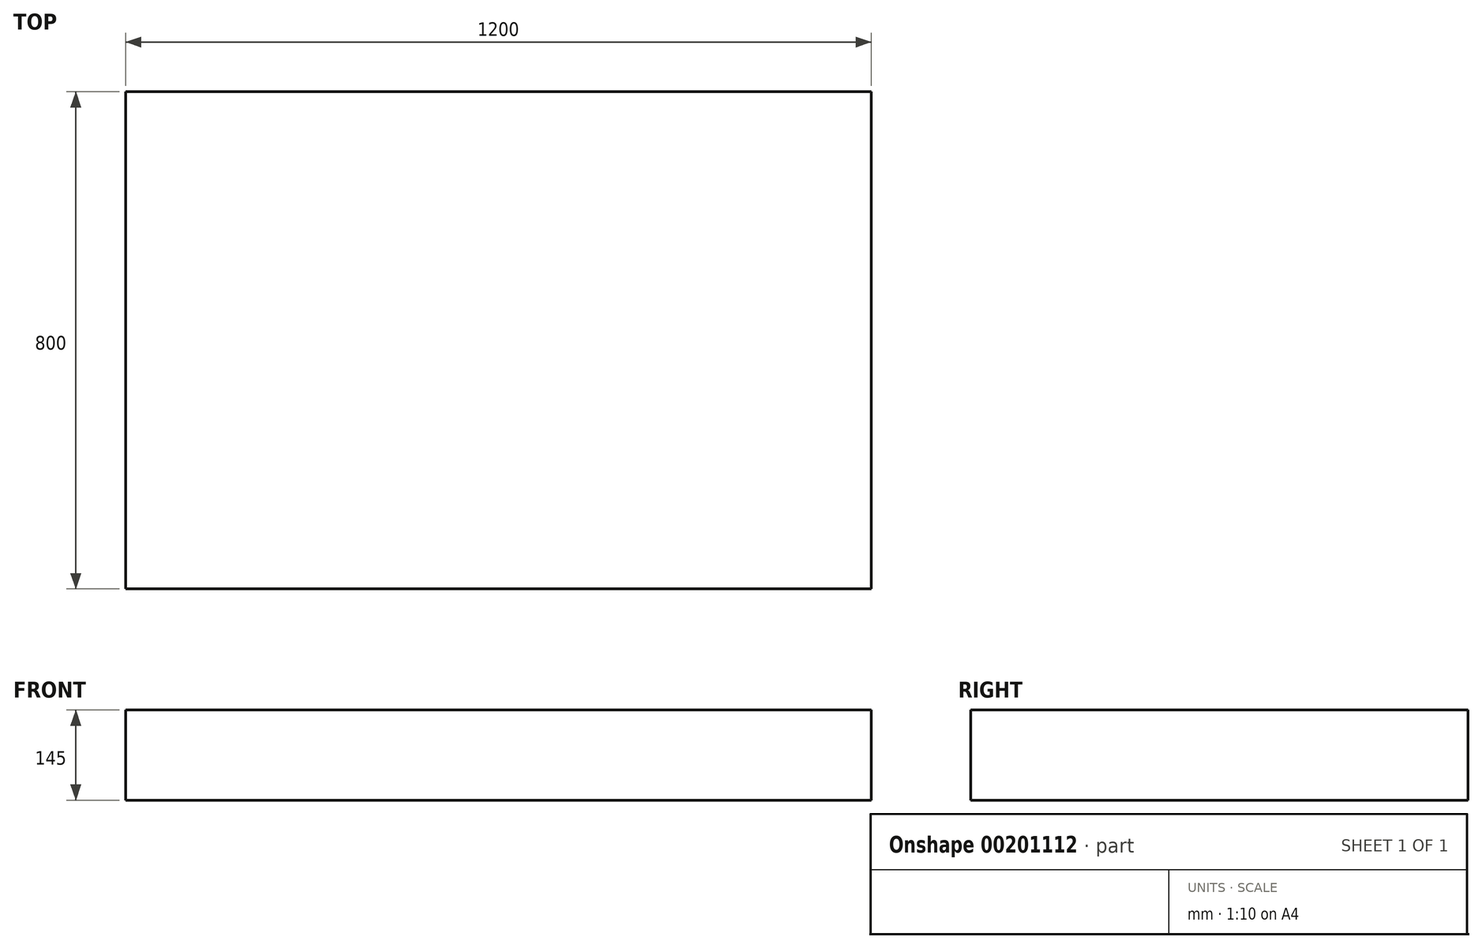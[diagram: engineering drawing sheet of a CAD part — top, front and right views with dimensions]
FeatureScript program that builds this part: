
annotation { "Feature Type Name" : "Feature", "Feature Type Description" : "" }
export const myFeature = defineFeature(function(context is Context, id is Id, definition is map)
    precondition{}
    {
        {
            var Q0;
            Q0=qCreatedBy(makeId("Top.planeOp"),FACE);
            var sketch = newSketch(context, id + "F0", { "sketchPlane" : qUnion([Q0])});
            skLineSegment(sketch, "E0.bottom", {"start": v(600, -400) * mm, "end": v(-600, -400) * mm});
            skLineSegment(sketch, "E0.top", {"start": v(600, 400) * mm, "end": v(-600, 400) * mm});
            skLineSegment(sketch, "E0.left", {"start": v(600, -400) * mm, "end": v(600, 400) * mm});
            skLineSegment(sketch, "E0.right", {"start": v(-600, -400) * mm, "end": v(-600, 400) * mm});
            skPoint(sketch, "E0.middle", {"position": v(0, 0) * mm});
            skSolve(sketch);
        }
        {
            var Q0;
            Q0=makeQuery(id+"F0.imprint","IMPRINT",FACE,{"disambiguationData":[TD([[makeQuery(id+"F0.imprint","IMPRINT",EDGE,{"derivedFrom":sQuery(id+"F0.wireOp",EDGE,"E0.bottom")}),-1.0]])]});
            extrude(context, id + "F1", {"entities" : qUnion([Q0]), "depth" : 145 * mm});
        }
    });
